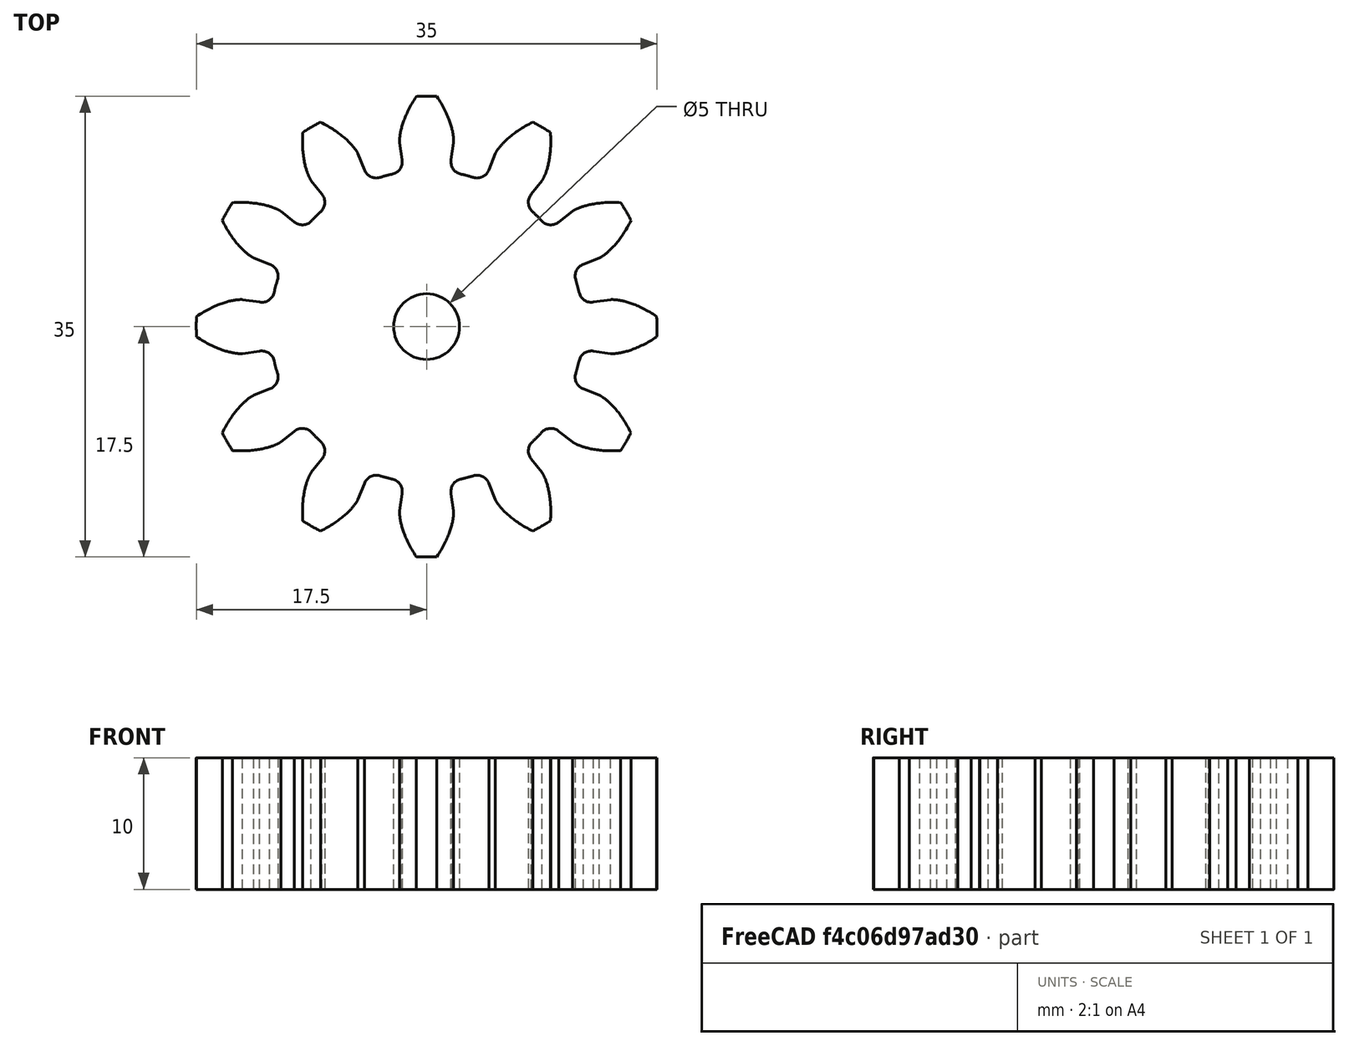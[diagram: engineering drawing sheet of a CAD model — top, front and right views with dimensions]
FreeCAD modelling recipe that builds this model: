
FCSTD DOCUMENT  (FreeCAD 1.0R39109 (Git))
Label: ギヤ30mm
License: All rights reserved
LicenseURL: https://en.wikipedia.org/wiki/All_rights_reserved
objects: Part::Part2DObjectPython×1, PartDesign::Pad×1, Sketcher::SketchObject×1, PartDesign::Pocket×1, PartDesign::Body×1
note: 10 computed .brp shape members not serialized (recipe doc carries the construction recipe); baked Part::Feature solids carry a one-line shape summary decoded from their .brp

FEATURE [Part::Part2DObjectPython] InvoluteGear  # Draft 2D object (typed FeaturePython)
  AddendumCoefficient = 1
  DedendumCoefficient = 1.25
  ExternalGear = true
  HighPrecision = true
  Modules = 2.5
  NumberOfTeeth = 12
  PressureAngle = 20
  ProfileShiftCoefficient = 0
  RootFilletCoefficient = 0.38
FEATURE [PartDesign::Pad] Pad
  Direction = (0,0,1)
  Length = 10
  Length2 = 10
  Profile = -> InvoluteGear
  ReferenceAxis = -> InvoluteGear [N_Axis]
  Refine = true
  Suppressed = false
  Type = 0
FEATURE [Sketcher::SketchObject] Sketch
  ArcFitTolerance = 1e-06
  AttachmentSupport = -> [Pad]
  FullyConstrained = true
  MakeInternals = false
  MapMode = 5
  Placement = pos=(0,0,10) rot=(0,0,1;0rad)
  sketch-geometry (1):
    g0: Circle CenterX=0 CenterY=0 CenterZ=0 NormalX=0 NormalY=0 NormalZ=1 AngleXU=0 Radius=2.5
  constraints (2):
    c: Coincident(g0,g-1)
    c: Diameter(g0) = 5
FEATURE [PartDesign::Pocket] Pocket
  BaseFeature = -> Pad
  Direction = (0,0,-1)
  Length = 5
  Length2 = 5
  Profile = -> Sketch
  ReferenceAxis = -> Sketch [N_Axis]
  Refine = true
  Suppressed = false
  Type = 1
FEATURE [PartDesign::Body] Body
  AllowCompound = false
  Group = -> [InvoluteGear,Pad,Sketch,Pocket]
  Origin = -> Origin
  Tip = -> Pocket
